# Revit family: 4430BF1U
name_source: partatom
category: Plumbing Fixtures
units: mm (PartAtom-declared; Revit-internal decimal feet)

## family parameters
Always vertical = Yes
Cut with Voids When Loaded = No
OmniClass Number = 23.45.00.00
OmniClass Title = Sanitary, Laundry, and Cleaning Equipment
Part Type = Normal
Room Calculation Point = No
Round Connector Dimension = Use Diameter
Shared = No
Work Plane-Based = No

## types (1)
- 4420BF1U
    Activation = Push Button
    Bubbler = Vandal Resistant
    CW Connection = No
    Description = Outdoor Tubular Bottle Filling Station Dual Station
    Filter = Non Filtered
    Fountain = OUTDOOR
    HW Connection = No
    Manufacturer = Elkay
    Material = Metal - Steel - Painted - Spruce Green
    Model = LK4420BF1U
    Mounting = Floor Mount
    Sanitary Flow = 0 GPM
    Sanitary Service Size Radius = 0' - 1 1/4"
    Type = Outdoor
    URL = http://elkayusa.com
    Vent Connection = No
    Waste Connection = No
    Water Service Flow = 0 GPM
    Water Service Flow Out = 0 GPM
    Water Service Radius = 0' - 0 3/8"
    Water Service Size Radius = 0' - 0 3/8"

## geometry (parser evidence)
native form markers: Sweep x7
no freeform markers — native parametric forms only
